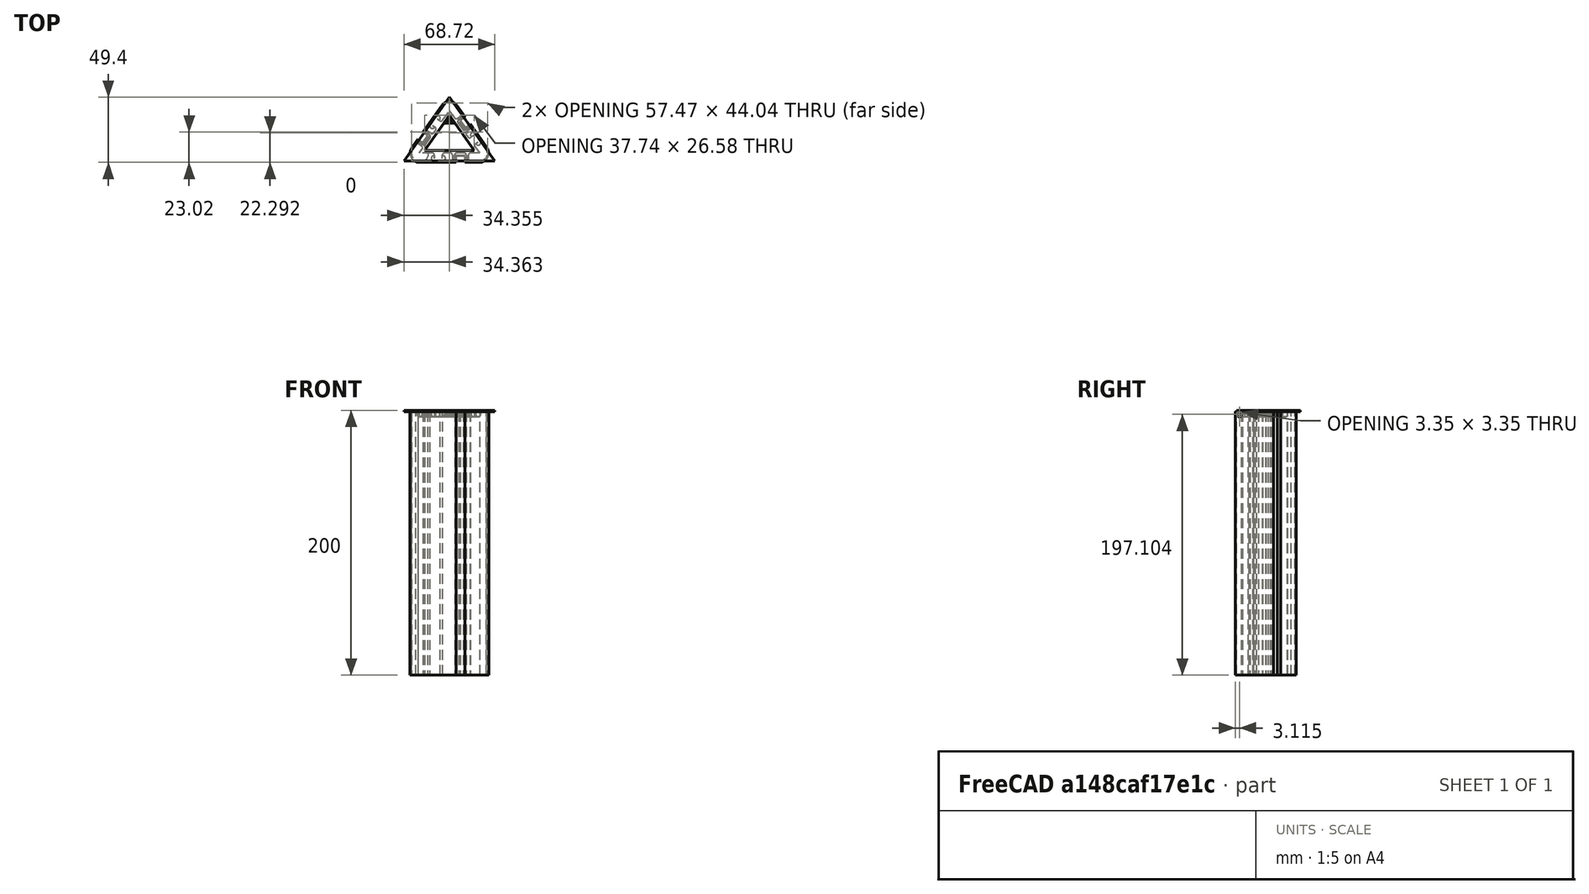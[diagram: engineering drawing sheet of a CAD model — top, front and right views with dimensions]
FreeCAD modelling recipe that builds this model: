
FCSTD DOCUMENT  (FreeCAD 0.20R29177 +233 (Git))
Label: tmp
License: All rights reserved
LicenseURL: http://en.wikipedia.org/wiki/All_rights_reserved
objects: Part::Part2DObjectPython×69, Part::Extrusion×29, Part::Cut×16, Part::MultiFuse×10, Part::Feature×9, Part::FeaturePython×5, App::DocumentObjectGroup×1, Part::Refine×1
note: 139 computed .brp shape members not serialized (recipe doc carries the construction recipe); baked Part::Feature solids carry a one-line shape summary decoded from their .brp

FEATURE [Part::Part2DObjectPython] Line219  label="Line220"  # Draft 2D object (typed FeaturePython)
  ChamferSize = 0
  Closed = false
  End = (11.2032,0.299498,-125.386)
  FilletRadius = 0
  Length = 52.293
  MakeFace = true
  Placement = pos=(-19.0727,42.9367,-125.386) rot=(0,0,1;3.14159rad)
  Points = (2) [(0,0,0),(-30.2758,42.6372,0)]
  Start = (-19.0727,42.9367,-125.386)
  Subdivisions = 0
FEATURE [Part::Part2DObjectPython] Line218  label="Line219"  # Draft 2D object (typed FeaturePython)
  ChamferSize = 0
  Closed = false
  End = (-19.0639,42.9441,-125.386)
  FilletRadius = 0
  Length = 52.293
  MakeFace = true
  Placement = pos=(-49.3293,0.299498,-125.386) rot=(0,0,1;3.14159rad)
  Points = (2) [(0,0,0),(-30.2654,-42.6446,0)]
  Start = (-49.3293,0.299498,-125.386)
  Subdivisions = 0
FEATURE [Part::Part2DObjectPython] Line217  label="Line218"  # Draft 2D object (typed FeaturePython)
  ChamferSize = 0
  Closed = false
  End = (11.2032,0.299498,-125.386)
  FilletRadius = 0
  Length = 60.5325
  MakeFace = true
  Placement = pos=(-49.3293,0.299498,-125.386) rot=(0,0,1;3.14159rad)
  Points = (2) [(0,0,0),(-60.5325,0,0)]
  Start = (-49.3293,0.299498,-125.386)
  Subdivisions = 0
FEATURE [Part::Feature] Fusion002009002005002004028003007012002019001002001013004001001
  shape: bbox 48.16 x 37.82 x 3.8 mm, 89 faces (baked)
FEATURE [Part::Feature] Face
  shape: bbox 3.474 x 4.892 x 3.8 mm, 1 faces, 0 solids (baked)
FEATURE [Part::Feature] Face001
  shape: bbox 3.473 x 4.893 x 3.8 mm, 1 faces, 0 solids (baked)
FEATURE [Part::Feature] Face002
  shape: bbox 6 x 2.493e-06 x 3.8 mm, 1 faces, 0 solids (baked)
FEATURE [Part::Feature] Face003
  Placement = pos=(1.78771e-08,-0.215137,-1.42e-14) rot=(0,0,1;0rad)
  shape: bbox 9.284 x 9.069 x 3.284 mm, 1 faces, 0 solids (baked)
FEATURE [Part::Feature] Face004
  Placement = pos=(0.175411,0.124556,0) rot=(0,0,1;0rad)
  shape: bbox 8.19 x 8.241 x 2.623e-06 mm, 1 faces, 0 solids (baked)
FEATURE [Part::Feature] Face005
  Placement = pos=(-0.175441,0.124513,0) rot=(0,0,1;0rad)
  shape: bbox 8.19 x 8.241 x 2.909e-06 mm, 1 faces, 0 solids (baked)
FEATURE [Part::Part2DObjectPython] Line220  label="Line221"  # Draft 2D object (typed FeaturePython)
  Area = 0
  ChamferSize = 0
  Closed = false
  End = (-53.4242,73.5903,-123.486)
  FilletRadius = 0
  Length = 75.6642
  MakeFace = true
  Placement = pos=(22.24,73.5903,-123.486) rot=(0,0.707107,-0.707107;3.14159rad)
  Points = (2) [(0,0,0),(75.6642,-3.1437e-06,-3.1437e-06)]
  Start = (22.24,73.5903,-123.486)
  Subdivisions = 0
FEATURE [Part::Part2DObjectPython] Line224  label="Line225"  # Draft 2D object (typed FeaturePython)
  Area = 0
  ChamferSize = 0
  Closed = true
  End = (-19.0714,121.994,-123.486)
  FilletRadius = 0
  Length = 59.3552
  MakeFace = true
  Placement = pos=(-19.0714,121.994,-123.486) rot=(-0.807496,-0.417103,0.417103;1.783rad)
  Points = (2) [(0,0,0),(0,0,0)]
  Start = (-19.0714,121.994,-123.486)
  Subdivisions = 0
FEATURE [Part::Part2DObjectPython] Line225  label="Line226"  # Draft 2D object (typed FeaturePython)
  Area = 0
  ChamferSize = 0
  Closed = false
  End = (-53.4242,73.5903,-123.486)
  FilletRadius = 0
  Length = 59.3552
  MakeFace = true
  Placement = pos=(-19.0714,121.994,-123.486) rot=(-0.807496,-0.417103,0.417103;1.783rad)
  Points = (2) [(0,0,0),(-59.3552,9.66338e-13,-1.20792e-12)]
  Start = (-19.0714,121.994,-123.486)
  Subdivisions = 0
FEATURE [Part::Part2DObjectPython] Line226  label="Line227"  # Draft 2D object (typed FeaturePython)
  Area = 0
  ChamferSize = 0
  Closed = true
  End = (-19.0714,121.994,-123.486)
  FilletRadius = 0
  Length = 0
  MakeFace = true
  Placement = pos=(-19.0714,121.994,-123.486) rot=(-0.807496,-0.417103,0.417103;1.783rad)
  Points = (2) [(0,0,0),(0,0,0)]
  Start = (-19.0714,121.994,-123.486)
  Subdivisions = 0
FEATURE [Part::Part2DObjectPython] Wire  # Draft 2D object (typed FeaturePython)
  Area = 1663.24
  ChamferSize = 0
  Closed = true
  End = (-19.0714,121.994,-123.486)
  FilletRadius = 0
  Length = 187.444
  MakeFace = true
  Placement = pos=(15.2992,73.5903,-123.486) rot=(0,0,1;0rad)
  Points = (3) [(0,0,0),(-68.7234,-6.72173e-12,-3.80851e-12),(-34.3706,48.4038,-3.85114e-12)]
  Start = (15.2992,73.5903,-123.486)
  Subdivisions = 0
FEATURE [Part::Extrusion] Extrusion006
  Base = -> Wire
  Dir = (-5.45e-14,3.88e-14,1)
  DirMode = 0
  FaceMakerClass = Part::FaceMakerBullseye
  LengthFwd = 0
  LengthRev = 0
  Solid = true
  Symmetric = false
FEATURE [Part::Part2DObjectPython] Wire001  # Draft 2D object (typed FeaturePython)
  Area = 501.678
  ChamferSize = 0
  Closed = true
  End = (-37.9365,81.5903,-123.486)
  FilletRadius = 0
  Length = 102.946
  MakeFace = true
  Placement = pos=(-19.0697,108.174,-123.486) rot=(1,0,0;3.14159rad)
  Points = (3) [(0,0,0),(18.8766,26.5837,2.18847e-12),(-18.8668,26.5837,1.56319e-13)]
  Start = (-19.0697,108.174,-123.486)
  Subdivisions = 0
FEATURE [Part::Extrusion] Extrusion007
  Base = -> Wire001
  Dir = (6.7e-15,-2.734e-13,57.9663)
  DirMode = 0
  FaceMakerClass = Part::FaceMakerBullseye
  LengthFwd = 0
  LengthRev = 0
  Solid = true
  Symmetric = false
FEATURE [Part::Cut] Cut
  Base = -> Extrusion006
  Tool = -> Extrusion007
FEATURE [Part::Part2DObjectPython] Rectangle  # Draft 2D object (typed FeaturePython)
  Area = 11871
  ChamferSize = 0
  Columns = 1
  FilletRadius = 0
  Height = 200
  Length = 59.3552
  MakeFace = true
  Placement = pos=(-53.4242,73.5903,-122.486) rot=(-0.807496,-0.417103,0.417103;1.783rad)
  Rows = 1
FEATURE [Part::Part2DObjectPython] Rectangle001  # Draft 2D object (typed FeaturePython)
  Area = 13744.7
  ChamferSize = 0
  Columns = 1
  FilletRadius = 0
  Height = 200
  Length = 68.7234
  MakeFace = true
  Placement = pos=(-53.4242,73.5903,-322.486) rot=(1,0,0;1.5708rad)
  Rows = 1
FEATURE [Part::Part2DObjectPython] Rectangle002  # Draft 2D object (typed FeaturePython)
  Area = 11813.7
  ChamferSize = 0
  Columns = 1
  FilletRadius = 0
  Height = 199
  Length = 59.3656
  MakeFace = true
  Placement = pos=(-19.0714,121.994,-123.486) rot=(-0.807581,0.417021,-0.417021;1.7829rad)
  Rows = 1
FEATURE [Part::Extrusion] Extrusion008
  Base = -> Rectangle001
  Dir = (9.82e-14,-1,4.1e-14)
  DirMode = 0
  FaceMakerClass = Part::FaceMakerBullseye
  LengthFwd = 0
  LengthRev = 0
  Solid = true
  Symmetric = false
FEATURE [Part::Extrusion] Extrusion009
  Base = -> Rectangle002
  Dir = (0.815352,0.578965,4.39e-14)
  DirMode = 0
  FaceMakerClass = Part::FaceMakerBullseye
  LengthFwd = 0
  LengthRev = 0
  Solid = true
  Symmetric = false
FEATURE [Part::Extrusion] Extrusion010
  Base = -> Rectangle
  Dir = (-0.815494,0.578766,-4.05e-14)
  DirMode = 0
  FaceMakerClass = Part::FaceMakerBullseye
  LengthFwd = 0
  LengthRev = 0
  Solid = true
  Symmetric = false
FEATURE [Part::MultiFuse] Fusion
  Shapes = -> [Extrusion010,Extrusion008,Extrusion009]
FEATURE [Part::Part2DObjectPython] Line228  label="Line229"  # Draft 2D object (typed FeaturePython)
  Area = 0
  ChamferSize = 0
  Closed = false
  End = (-38.3867,87.0032,-123.486)
  FilletRadius = 0
  Length = 1
  MakeFace = true
  Placement = pos=(-38.9655,86.1877,-123.486) rot=(0,0,1;0.953582rad)
  Points = (2) [(0,0,0),(1,-2.84217e-14,-2.84217e-14)]
  Start = (-38.9655,86.1877,-123.486)
  Subdivisions = 0
FEATURE [Part::Part2DObjectPython] Line230  label="Line231"  # Draft 2D object (typed FeaturePython)
  Area = 0
  ChamferSize = 0
  Closed = false
  End = (-34.6247,92.3039,-123.486)
  FilletRadius = 0
  Length = 1
  MakeFace = true
  Placement = pos=(-34.046,93.1194,-123.486) rot=(0,0,1;0.953582rad)
  Points = (2) [(0,0,0),(-1,5.68434e-14,2.41585e-13)]
  Start = (-34.046,93.1194,-123.486)
  Subdivisions = 0
FEATURE [Part::Part2DObjectPython] Rectangle006  # Draft 2D object (typed FeaturePython)
  Area = 29.25
  ChamferSize = 0
  Columns = 1
  FilletRadius = 0
  Height = 4.5
  Length = 6.5
  MakeFace = true
  Placement = pos=(-39.2022,87.582,-123.486) rot=(0,0,1;0.953582rad)
  Rows = 1
FEATURE [Part::Extrusion] Extrusion011
  Base = -> Rectangle006
  Dir = (1.04812e-11,6.8116e-12,-353.777)
  DirMode = 0
  FaceMakerClass = Part::FaceMakerBullseye
  LengthFwd = 0
  LengthRev = 0
  Solid = true
  Symmetric = false
FEATURE [Part::Cut] Cut001
  Base = -> Fusion
  Tool = -> Extrusion011
FEATURE [Part::Part2DObjectPython] Rectangle007  # Draft 2D object (typed FeaturePython)
  Area = 21476.5
  ChamferSize = 0
  Columns = 1
  FilletRadius = 0
  Height = 94.2802
  Length = 227.794
  MakeFace = true
  Placement = pos=(-179.415,55.7642,-123.486) rot=(0,0,1;0rad)
  Rows = 1
FEATURE [Part::FeaturePython] Slice  # WARN: FeaturePython — macro-defined, semantics opaque (R4)
  Base = -> Cut001
  Mode = 1
  Tolerance = 0
  Tools = -> [Rectangle007]
FEATURE [Part::FeaturePython] Slice_child1  label="Slice.1"  # WARN: FeaturePython — macro-defined, semantics opaque (R4)
  Base = -> Slice
  FilterType = 1
  Invert = false
  OverrideMaxVal = 0
  WindowFrom = 80
  WindowTo = 100
  items = 1
FEATURE [Part::FeaturePython] Slice_child2  label="Slice.2"  # WARN: FeaturePython — macro-defined, semantics opaque (R4)
  Base = -> Slice
  FilterType = 1
  Invert = false
  OverrideMaxVal = 0
  WindowFrom = 80
  WindowTo = 100
  items = 2
FEATURE [Part::FeaturePython] Slice_child4  label="Slice.4"  # WARN: FeaturePython — macro-defined, semantics opaque (R4)
  Base = -> Slice
  FilterType = 1
  Invert = false
  OverrideMaxVal = 0
  WindowFrom = 80
  WindowTo = 100
  items = 4
FEATURE [Part::FeaturePython] Slice_child5  label="Slice.5"  # WARN: FeaturePython — macro-defined, semantics opaque (R4)
  Base = -> Slice
  FilterType = 1
  Invert = false
  OverrideMaxVal = 0
  WindowFrom = 80
  WindowTo = 100
  items = 5
FEATURE [Part::Part2DObjectPython] Wire002  # Draft 2D object (typed FeaturePython)
  Area = 17.5
  ChamferSize = 0
  Closed = true
  End = (-39.11,95.4871,-123.486)
  FilletRadius = 0
  Length = 37
  MakeFace = true
  Placement = pos=(-38.5312,96.3026,-123.486) rot=(0,0,1;0.953582rad)
  Points = (8) [(0,0,0),(1.42109e-13,-5.5,-2.13163e-13),(-8.5,-5.5,-2.41585e-13),(-8.5,-2.70006e-13,2.70006e-13),(-7.5,-2.70006e-13,-2.55795e-13),+3 more]
  Start = (-38.5312,96.3026,-123.486)
  Subdivisions = 0
FEATURE [Part::Extrusion] Extrusion012
  Base = -> Wire002
  Dir = (-2.929e-13,9.0155e-12,-199)
  DirMode = 0
  FaceMakerClass = Part::FaceMakerBullseye
  LengthFwd = 0
  LengthRev = 0
  Solid = true
  Symmetric = false
FEATURE [Part::Part2DObjectPython] Line233  label="Line234"  # Draft 2D object (typed FeaturePython)
  Area = 0
  ChamferSize = 0
  Closed = false
  End = (-12.1534,104.479,-123.486)
  FilletRadius = 0
  Length = 1
  MakeFace = true
  Placement = pos=(-11.5744,103.664,-123.486) rot=(0,0,-1;0.953337rad)
  Points = (2) [(0,0,0),(-1,4.26326e-14,2.13163e-13)]
  Start = (-11.5744,103.664,-123.486)
  Subdivisions = 0
FEATURE [Part::Part2DObjectPython] Line234  label="Line235"  # Draft 2D object (typed FeaturePython)
  Area = 0
  ChamferSize = 0
  Closed = false
  End = (-7.81115,98.3639,-123.486)
  FilletRadius = 0
  Length = 1
  MakeFace = true
  Placement = pos=(-7.23218,97.5486,-123.486) rot=(0,0,-1;0.953337rad)
  Points = (2) [(0,0,0),(-1,4.9738e-14,2.13163e-13)]
  Start = (-7.23218,97.5486,-123.486)
  Subdivisions = 0
FEATURE [Part::Part2DObjectPython] Line237  label="Line238"  # Draft 2D object (typed FeaturePython)
  Area = 0
  ChamferSize = 0
  Closed = false
  End = (-7.08999,106.848,-123.486)
  FilletRadius = 0
  Length = 5.5
  MakeFace = true
  Placement = pos=(-11.5744,103.664,-123.486) rot=(0,0,-1;0.953337rad)
  Points = (2) [(0,0,0),(-1.56319e-13,5.5,-1.59162e-12)]
  Start = (-11.5744,103.664,-123.486)
  Subdivisions = 0
FEATURE [Part::Part2DObjectPython] Line238  label="Line239"  # Draft 2D object (typed FeaturePython)
  Area = 0
  ChamferSize = 0
  Closed = false
  End = (-3.32671,101.548,-123.486)
  FilletRadius = 0
  Length = 5.5
  MakeFace = true
  Placement = pos=(-7.81115,98.3639,-123.486) rot=(0,0,-1;0.953337rad)
  Points = (2) [(0,0,0),(-1.84741e-13,5.5,-2.25953e-12)]
  Start = (-7.81115,98.3639,-123.486)
  Subdivisions = 0
FEATURE [Part::Part2DObjectPython] Line239  label="Line240"  # Draft 2D object (typed FeaturePython)
  Area = 0
  ChamferSize = 0
  Closed = false
  End = (-3.5631,100.154,-123.486)
  FilletRadius = 0
  Length = 4.5
  MakeFace = true
  Placement = pos=(-7.23218,97.5486,-123.486) rot=(0,0,-1;0.953337rad)
  Points = (2) [(0,0,0),(-2.27374e-13,4.5,1.27898e-13)]
  Start = (-7.23218,97.5486,-123.486)
  Subdivisions = 0
FEATURE [Part::Part2DObjectPython] Line240  label="Line241"  # Draft 2D object (typed FeaturePython)
  Area = 0
  ChamferSize = 0
  Closed = false
  End = (-8.48431,107.084,-123.486)
  FilletRadius = 0
  Length = 4.5
  MakeFace = true
  Placement = pos=(-12.1534,104.479,-123.486) rot=(0,0,-1;0.953337rad)
  Points = (2) [(0,0,0),(-2.27374e-13,4.5,-2.27374e-13)]
  Start = (-12.1534,104.479,-123.486)
  Subdivisions = 0
FEATURE [Part::Part2DObjectPython] Rectangle008  # Draft 2D object (typed FeaturePython)
  Area = 35.75
  ChamferSize = 0
  Columns = 1
  FilletRadius = 0
  Height = 5.5
  Length = 6.5
  MakeFace = true
  Placement = pos=(-11.5744,103.664,-123.486) rot=(0,0,-1;0.953337rad)
  Rows = 1
FEATURE [Part::Extrusion] Extrusion
  Base = -> Rectangle008
  Dir = (8.0766e-12,-3.5936e-12,-250.551)
  DirMode = 0
  FaceMakerClass = Part::FaceMakerBullseye
  LengthFwd = 0
  LengthRev = 0
  Solid = true
  Symmetric = false
FEATURE [Part::Cut] Cut002
  Base = -> Slice_child5
  Tool = -> Extrusion
FEATURE [Part::Part2DObjectPython] Wire003  # Draft 2D object (typed FeaturePython)
  Area = 15.5
  ChamferSize = 0
  Closed = true
  End = (-3.5631,100.154,-123.486)
  FilletRadius = 0
  Length = 33
  MakeFace = true
  Placement = pos=(-7.23218,97.5486,-123.486) rot=(0,0,1;0rad)
  Points = (8) [(0,0,0),(-4.92121,6.93049,-1.84741e-13),(-1.25212,9.53584,-3.2685e-13),(-0.673157,8.72049,-1.02318e-12),(-3.52689,6.69411,-6.39488e-13),+3 more]
  Start = (-7.23218,97.5486,-123.486)
  Subdivisions = 0
FEATURE [Part::Extrusion] Extrusion013
  Base = -> Wire003
  Dir = (-7.6149e-12,-1.43446e-11,-199)
  DirMode = 0
  FaceMakerClass = Part::FaceMakerBullseye
  LengthFwd = 0
  LengthRev = 0
  Solid = true
  Symmetric = false
FEATURE [Part::Part2DObjectPython] Line221  label="Line222"  # Draft 2D object (typed FeaturePython)
  Area = 0
  ChamferSize = 0
  Closed = false
  End = (15.2992,73.5903,-123.486)
  FilletRadius = 0
  Length = 100
  MakeFace = true
  Placement = pos=(-42.5973,155.125,-123.486) rot=(-0.807581,0.417021,-0.417021;1.7829rad)
  Points = (2) [(0,0,0),(100,-8.1144e-12,1.86873e-12)]
  Start = (-42.5973,155.125,-123.486)
  Subdivisions = 0
FEATURE [Part::Part2DObjectPython] Line242  label="Line243"  # Draft 2D object (typed FeaturePython)
  Area = 0
  ChamferSize = 0
  Closed = false
  End = (-13.9631,78.0903,-123.486)
  FilletRadius = 0
  Length = 1
  MakeFace = true
  Placement = pos=(-14.9631,78.0903,-123.486) rot=(0,0,1;3.14159rad)
  Points = (2) [(0,0,0),(-1,-4.15481e-08,2.27374e-13)]
  Start = (-14.9631,78.0903,-123.486)
  Subdivisions = 0
FEATURE [Part::Part2DObjectPython] Line243  label="Line244"  # Draft 2D object (typed FeaturePython)
  Area = 0
  ChamferSize = 0
  Closed = false
  End = (-6.46309,78.0903,-123.486)
  FilletRadius = 0
  Length = 1
  MakeFace = true
  Placement = pos=(-7.46309,78.0903,-123.486) rot=(0,0,1;3.14159rad)
  Points = (2) [(0,0,0),(-1,-4.15481e-08,2.27374e-13)]
  Start = (-7.46309,78.0903,-123.486)
  Subdivisions = 0
FEATURE [Part::Part2DObjectPython] Line  # Draft 2D object (typed FeaturePython)
  Area = 0
  ChamferSize = 0
  Closed = false
  End = (-14.9631,73.5903,-123.486)
  FilletRadius = 0
  Length = 4.5
  MakeFace = true
  Placement = pos=(-14.9631,78.0903,-123.486) rot=(0,0,1;3.14159rad)
  Points = (2) [(0,0,0),(1.86967e-07,4.5,-1.40687e-12)]
  Start = (-14.9631,78.0903,-123.486)
  Subdivisions = 0
FEATURE [Part::Part2DObjectPython] Line244  label="Line245"  # Draft 2D object (typed FeaturePython)
  Area = 0
  ChamferSize = 0
  Closed = false
  End = (-6.46309,73.5903,-123.486)
  FilletRadius = 0
  Length = 4.5
  MakeFace = true
  Placement = pos=(-6.46309,78.0903,-123.486) rot=(0,0,1;3.14159rad)
  Points = (2) [(0,0,0),(1.86967e-07,4.5,-1.62004e-12)]
  Start = (-6.46309,78.0903,-123.486)
  Subdivisions = 0
FEATURE [Part::Part2DObjectPython] Line245  label="Line246"  # Draft 2D object (typed FeaturePython)
  Area = 0
  ChamferSize = 0
  Closed = false
  End = (-7.46309,72.5903,-123.486)
  FilletRadius = 0
  Length = 5.5
  MakeFace = true
  Placement = pos=(-7.46309,78.0903,-123.486) rot=(0,0,1;3.14159rad)
  Points = (2) [(0,0,0),(2.28515e-07,5.5,5.25802e-13)]
  Start = (-7.46309,78.0903,-123.486)
  Subdivisions = 0
FEATURE [Part::Part2DObjectPython] Line246  label="Line247"  # Draft 2D object (typed FeaturePython)
  Area = 0
  ChamferSize = 0
  Closed = false
  End = (-13.9631,72.5903,-123.486)
  FilletRadius = 0
  Length = 5.5
  MakeFace = true
  Placement = pos=(-13.9631,78.0903,-123.486) rot=(0,0,1;3.14159rad)
  Points = (2) [(0,0,0),(2.28515e-07,5.5,0)]
  Start = (-13.9631,78.0903,-123.486)
  Subdivisions = 0
FEATURE [Part::Part2DObjectPython] Line247  label="Line248"  # Draft 2D object (typed FeaturePython)
  Area = 0
  ChamferSize = 0
  Closed = false
  End = (-14.4631,77.0903,-123.486)
  FilletRadius = 0
  Length = 1
  MakeFace = true
  Placement = pos=(-14.4631,78.0903,-123.486) rot=(0,0,1;3.14159rad)
  Points = (2) [(0,0,0),(4.15481e-08,1,-3.12639e-13)]
  Start = (-14.4631,78.0903,-123.486)
  Subdivisions = 0
FEATURE [Part::Part2DObjectPython] Line249  label="Line250"  # Draft 2D object (typed FeaturePython)
  Area = 0
  ChamferSize = 0
  Closed = false
  End = (-13.9631,77.0903,-123.486)
  FilletRadius = 0
  Length = 6.5
  MakeFace = true
  Placement = pos=(-7.46309,77.0903,-123.486) rot=(0,0,1;3.14159rad)
  Points = (2) [(0,0,0),(6.5,-2.70063e-07,1.84741e-13)]
  Start = (-7.46309,77.0903,-123.486)
  Subdivisions = 0
FEATURE [Part::Part2DObjectPython] Rectangle009  # Draft 2D object (typed FeaturePython)
  Area = 29.25
  ChamferSize = 0
  Columns = 1
  FilletRadius = 0
  Height = 4.5
  Length = 6.5
  MakeFace = true
  Placement = pos=(-7.46309,77.0903,-123.486) rot=(0,0,1;3.14159rad)
  Rows = 1
FEATURE [Part::Extrusion] Extrusion014
  Base = -> Rectangle009
  Dir = (-9.5338e-12,8.731e-13,-292.184)
  DirMode = 0
  FaceMakerClass = Part::FaceMakerBullseye
  LengthFwd = 0
  LengthRev = 0
  Solid = true
  Symmetric = false
FEATURE [Part::Cut] Cut003
  Base = -> Slice_child4
  Tool = -> Extrusion014
FEATURE [Part::Part2DObjectPython] Wire004  # Draft 2D object (typed FeaturePython)
  Area = 15.5
  ChamferSize = 0
  Closed = true
  End = (-14.9631,73.5903,-123.486)
  FilletRadius = 0
  Length = 33
  MakeFace = true
  Placement = pos=(-14.9631,78.0903,-123.486) rot=(0,0,1;3.14159rad)
  Points = (8) [(0,0,0),(-8.5,2.18128e-07,-1.27898e-13),(-8.5,4.5,-1.74794e-12),(-7.5,4.5,9.9476e-14),(-7.5,1,-2.13163e-13),(-1,1,1.7053e-13),(-1,4.5,1.56319e-13),+1 more]
  Start = (-14.9631,78.0903,-123.486)
  Subdivisions = 0
FEATURE [Part::Extrusion] Extrusion015
  Base = -> Wire004
  Dir = (-6.1347e-12,3.55999e-11,-199)
  DirMode = 0
  FaceMakerClass = Part::FaceMakerBullseye
  LengthFwd = 0
  LengthRev = 0
  Solid = true
  Symmetric = false
FEATURE [Part::MultiFuse] Fusion002009002005002004028003007012002019001002001013004001002
  Shapes = -> [Extrusion015,Cut003,Extrusion012,Extrusion013]
FEATURE [Part::MultiFuse] Fusion002009002005002004028003007012002019001002001013004001003
  Shapes = -> [Fusion002009002005002004028003007012002019001002001013004001002,Cut002,Slice_child1]
FEATURE [Part::MultiFuse] Fusion002009002005002004028003007012002019001002001013004001004
  Shapes = -> [Fusion002009002005002004028003007012002019001002001013004001003,Slice_child2]
FEATURE [Part::Part2DObjectPython] Wire005  # Draft 2D object (typed FeaturePython)
  Area = 0.407747
  ChamferSize = 0
  Closed = true
  End = (-53.4242,73.5903,-123.486)
  FilletRadius = 0
  Length = 3.77694
  MakeFace = true
  Placement = pos=(-54.2397,74.169,-123.486) rot=(0,0,-1;0.617214rad)
  Points = (3) [(0,0,0),(1.57877,-0.815494,0),(1,-7.10543e-15,0)]
  Start = (-54.2397,74.169,-123.486)
  Subdivisions = 0
FEATURE [Part::Part2DObjectPython] Wire006  # Draft 2D object (typed FeaturePython)
  Area = 0.407676
  ChamferSize = 0
  Closed = true
  End = (15.2992,73.5903,-123.486)
  FilletRadius = 0
  Length = 3.77706
  MakeFace = true
  Placement = pos=(16.1146,74.1692,-123.486) rot=(0,0,-1;0.617214rad)
  Points = (3) [(0,0,0),(0.248936,-1.75953,2.77112e-12),(-0.329829,-0.944041,-4.26326e-14)]
  Start = (16.1146,74.1692,-123.486)
  Subdivisions = 0
FEATURE [Part::Part2DObjectPython] Wire007  # Draft 2D object (typed FeaturePython)
  Area = 0.47202
  ChamferSize = 0
  Closed = true
  End = (-19.0714,121.994,-123.486)
  FilletRadius = 0
  Length = 3.63085
  MakeFace = true
  Placement = pos=(-19.8869,122.573,-123.486) rot=(0,0,-1;0.617214rad)
  Points = (3) [(0,0,0),(1.32983,0.944041,-1.73372e-12),(1,9.9476e-13,-1.77636e-12)]
  Start = (-19.8869,122.573,-123.486)
  Subdivisions = 0
FEATURE [Part::Extrusion] Extrusion016
  Base = -> Wire006
  Dir = (4.08027e-10,-5.59542e-10,-199)
  DirMode = 0
  FaceMakerClass = Part::FaceMakerBullseye
  LengthFwd = 0
  LengthRev = 0
  Solid = true
  Symmetric = false
FEATURE [Part::Extrusion] Extrusion017
  Base = -> Wire005
  Dir = (2.25e-14,3.937e-13,-199)
  DirMode = 0
  FaceMakerClass = Part::FaceMakerBullseye
  LengthFwd = 0
  LengthRev = 0
  Solid = true
  Symmetric = false
FEATURE [Part::Extrusion] Extrusion018
  Base = -> Wire007
  Dir = (-2.11569e-10,3.1303e-10,-199)
  DirMode = 0
  FaceMakerClass = Part::FaceMakerBullseye
  LengthFwd = 0
  LengthRev = 0
  Solid = true
  Symmetric = false
FEATURE [Part::MultiFuse] Fusion002009002005002004028003007012002019001002001013004001005
  Shapes = -> [Fusion002009002005002004028003007012002019001002001013004001004,Extrusion017]
FEATURE [Part::MultiFuse] Fusion002009002005002004028003007012002019001002001013004001006
  Shapes = -> [Fusion002009002005002004028003007012002019001002001013004001005,Extrusion018]
FEATURE [Part::MultiFuse] Fusion002009002005002004028003007012002019001002001013004001007
  Shapes = -> [Fusion002009002005002004028003007012002019001002001013004001006,Extrusion016]
FEATURE [Part::Part2DObjectPython] Circle  # Draft 2D object (typed FeaturePython)
  Area = 3.14159
  FirstAngle = 0
  LastAngle = 0
  MakeFace = true
  Placement = pos=(15.2992,73.5903,-123.486) rot=(0,0,1;0rad)
  Radius = 1
FEATURE [Part::Part2DObjectPython] Circle001  # Draft 2D object (typed FeaturePython)
  Area = 3.14159
  FirstAngle = 0
  LastAngle = 0
  MakeFace = true
  Placement = pos=(-53.4242,73.5903,-123.486) rot=(0,0,1;0rad)
  Radius = 1
FEATURE [Part::Part2DObjectPython] Circle002  # Draft 2D object (typed FeaturePython)
  Area = 3.14159
  FirstAngle = 0
  LastAngle = 0
  MakeFace = true
  Placement = pos=(-19.0714,121.994,-123.486) rot=(0,0,1;0rad)
  Radius = 1
FEATURE [Part::Part2DObjectPython] Circle003  # Draft 2D object (typed FeaturePython)
  Area = 113.097
  FirstAngle = 0
  LastAngle = 0
  MakeFace = true
  Placement = pos=(3.67995,79.5903,-123.486) rot=(0,0,1;0rad)
  Radius = 6
FEATURE [Part::Part2DObjectPython] Circle004  # Draft 2D object (typed FeaturePython)
  Area = 153.938
  FirstAngle = 0
  LastAngle = 0
  MakeFace = true
  Placement = pos=(3.67995,79.5903,-123.486) rot=(0,0,1;0rad)
  Radius = 7
FEATURE [Part::Extrusion] Extrusion022
  Base = -> Circle004
  Dir = (-1.871e-13,2.726e-13,-199)
  DirMode = 0
  FaceMakerClass = Part::FaceMakerBullseye
  LengthFwd = 0
  LengthRev = 0
  Solid = true
  Symmetric = false
FEATURE [Part::Extrusion] Extrusion023
  Base = -> Circle003
  Dir = (-3.395e-13,4.948e-13,-361.137)
  DirMode = 0
  FaceMakerClass = Part::FaceMakerBullseye
  LengthFwd = 0
  LengthRev = 0
  Solid = true
  Symmetric = false
FEATURE [Part::Cut] Cut004
  Base = -> Extrusion022
  Tool = -> Extrusion023
FEATURE [Part::Part2DObjectPython] Line250  label="Line251"  # Draft 2D object (typed FeaturePython)
  Area = 0
  ChamferSize = 0
  Closed = false
  End = (9.38741,83.643,-322.486)
  FilletRadius = 0
  Length = 7
  MakeFace = true
  Placement = pos=(3.67995,79.5903,-322.486) rot=(1,0,0;3.14159rad)
  Points = (2) [(0,0,0),(5.70746,-4.05276,6.9349e-12)]
  Start = (3.67995,79.5903,-322.486)
  Subdivisions = 0
FEATURE [Part::Part2DObjectPython] Line251  label="Line252"  # Draft 2D object (typed FeaturePython)
  Area = 0
  ChamferSize = 0
  Closed = false
  End = (3.67995,72.5903,-322.486)
  FilletRadius = 0
  Length = 7
  MakeFace = true
  Placement = pos=(3.67995,79.5903,-322.486) rot=(1,0,0;3.14159rad)
  Points = (2) [(0,0,0),(-8.40923e-11,7,2.84217e-13)]
  Start = (3.67995,79.5903,-322.486)
  Subdivisions = 0
FEATURE [Part::Part2DObjectPython] Wire008  # Draft 2D object (typed FeaturePython)
  Area = 133.226
  ChamferSize = 0
  Closed = true
  End = (9.38741,83.643,-322.486)
  FilletRadius = 0
  Length = 57.0494
  MakeFace = true
  Placement = pos=(3.67995,72.5903,-322.486) rot=(1,0,0;3.14159rad)
  Points = (3) [(0,0,0),(21.9308,4.215,0),(5.70746,-11.0528,6.65068e-12)]
  Start = (3.67995,72.5903,-322.486)
  Subdivisions = 0
FEATURE [Part::Extrusion] Extrusion024
  Base = -> Wire008
  Dir = (1.52045e-11,1.77155e-10,301.099)
  DirMode = 0
  FaceMakerClass = Part::FaceMakerBullseye
  LengthFwd = 0
  LengthRev = 0
  Solid = true
  Symmetric = false
FEATURE [Part::Cut] Cut005
  Base = -> Fusion002009002005002004028003007012002019001002001013004001007
  Tool = -> Extrusion024
FEATURE [Part::Part2DObjectPython] Line252  label="Line253"  # Draft 2D object (typed FeaturePython)
  Area = 0
  ChamferSize = 0
  Closed = false
  End = (-24.7766,115.683,-123.486)
  FilletRadius = 0
  Length = 7
  MakeFace = true
  Placement = pos=(-19.0701,111.629,-123.486) rot=(0,0,1;0rad)
  Points = (2) [(0,0,0),(-5.70651,4.0541,0)]
  Start = (-19.0701,111.629,-123.486)
  Subdivisions = 0
FEATURE [Part::Part2DObjectPython] Line253  label="Line254"  # Draft 2D object (typed FeaturePython)
  Area = 0
  ChamferSize = 0
  Closed = false
  End = (-13.3627,115.682,-123.486)
  FilletRadius = 0
  Length = 7
  MakeFace = true
  Placement = pos=(-19.0701,111.629,-123.486) rot=(0,0,1;0rad)
  Points = (2) [(0,0,0),(5.70746,4.05276,-1.10845e-12)]
  Start = (-19.0701,111.629,-123.486)
  Subdivisions = 0
FEATURE [Part::Part2DObjectPython] Line254  label="Line255"  # Draft 2D object (typed FeaturePython)
  Area = 0
  ChamferSize = 0
  Closed = false
  End = (-41.8084,72.5903,-123.486)
  FilletRadius = 0
  Length = 7
  MakeFace = true
  Placement = pos=(-41.8084,79.5903,-123.486) rot=(0,0,1;0rad)
  Points = (2) [(0,0,0),(6.82121e-13,-7,0)]
  Start = (-41.8084,79.5903,-123.486)
  Subdivisions = 0
FEATURE [Part::Part2DObjectPython] Line255  label="Line256"  # Draft 2D object (typed FeaturePython)
  Area = 0
  ChamferSize = 0
  Closed = false
  End = (-47.5168,83.6416,-123.486)
  FilletRadius = 0
  Length = 7
  MakeFace = true
  Placement = pos=(-41.8084,79.5903,-123.486) rot=(0,0,1;0rad)
  Points = (2) [(0,0,0),(-5.70846,4.05136,9.9476e-14)]
  Start = (-41.8084,79.5903,-123.486)
  Subdivisions = 0
FEATURE [Part::Part2DObjectPython] Wire009  # Draft 2D object (typed FeaturePython)
  Area = 116.676
  ChamferSize = 0
  Closed = true
  End = (-41.8084,72.5903,-123.486)
  FilletRadius = 0
  Length = 51.9976
  MakeFace = true
  Placement = pos=(-47.5168,83.6416,-123.486) rot=(0,0,1;0rad)
  Points = (3) [(0,0,0),(-13.4387,-14.8614,-1.42109e-14),(5.70846,-11.0514,-8.52651e-14)]
  Start = (-47.5168,83.6416,-123.486)
  Subdivisions = 0
FEATURE [Part::Part2DObjectPython] Wire010  # Draft 2D object (typed FeaturePython)
  Area = 64.0628
  ChamferSize = 0
  Closed = true
  End = (-13.3627,115.682,-123.486)
  FilletRadius = 0
  Length = 36.6012
  MakeFace = true
  Placement = pos=(-24.7766,115.683,-123.486) rot=(0,0,1;0rad)
  Points = (3) [(0,0,0),(5.87287,11.2246,1.42109e-14),(11.414,-0.0013408,-1.12266e-12)]
  Start = (-24.7766,115.683,-123.486)
  Subdivisions = 0
FEATURE [Part::Extrusion] Extrusion025
  Base = -> Wire010
  Dir = (-1.97591e-11,1.07649e-11,-199)
  DirMode = 0
  FaceMakerClass = Part::FaceMakerBullseye
  LengthFwd = 0
  LengthRev = 0
  Solid = true
  Symmetric = false
FEATURE [Part::Extrusion] Extrusion026
  Base = -> Wire009
  Dir = (-1.1338e-12,1.319e-12,-199)
  DirMode = 0
  FaceMakerClass = Part::FaceMakerBullseye
  LengthFwd = 0
  LengthRev = 0
  Solid = true
  Symmetric = false
FEATURE [Part::Cut] Cut006
  Base = -> Cut005
  Tool = -> Extrusion026
FEATURE [Part::Cut] Cut007
  Base = -> Cut006
  Tool = -> Extrusion025
FEATURE [Part::Part2DObjectPython] Circle005  # Draft 2D object (typed FeaturePython)
  Area = 153.938
  FirstAngle = 0
  LastAngle = 0
  MakeFace = true
  Placement = pos=(-41.8084,79.5903,-123.486) rot=(0,0,1;0rad)
  Radius = 7
FEATURE [Part::Part2DObjectPython] Circle006  # Draft 2D object (typed FeaturePython)
  Area = 113.097
  FirstAngle = 0
  LastAngle = 0
  MakeFace = true
  Placement = pos=(-41.8084,79.5903,-123.486) rot=(0,0,1;0rad)
  Radius = 6
FEATURE [Part::Part2DObjectPython] Circle007  # Draft 2D object (typed FeaturePython)
  Area = 153.938
  FirstAngle = 0
  LastAngle = 0
  MakeFace = true
  Placement = pos=(-19.0701,111.629,-123.486) rot=(0,0,1;0rad)
  Radius = 7
FEATURE [Part::Part2DObjectPython] Circle008  # Draft 2D object (typed FeaturePython)
  Area = 113.097
  FirstAngle = 0
  LastAngle = 0
  MakeFace = true
  Placement = pos=(-19.0701,111.629,-123.486) rot=(0,0,1;0rad)
  Radius = 6
FEATURE [Part::Extrusion] Extrusion027
  Base = -> Circle007
  Dir = (-1.871e-13,2.726e-13,-199)
  DirMode = 0
  FaceMakerClass = Part::FaceMakerBullseye
  LengthFwd = 0
  LengthRev = 0
  Solid = true
  Symmetric = false
FEATURE [Part::Extrusion] Extrusion028
  Base = -> Circle005
  Dir = (-1.871e-13,2.726e-13,-199)
  DirMode = 0
  FaceMakerClass = Part::FaceMakerBullseye
  LengthFwd = 0
  LengthRev = 0
  Solid = true
  Symmetric = false
FEATURE [Part::Extrusion] Extrusion029
  Base = -> Circle006
  Dir = (-9.882e-13,1.4403e-12,-1051.29)
  DirMode = 0
  FaceMakerClass = Part::FaceMakerBullseye
  LengthFwd = 0
  LengthRev = 0
  Solid = true
  Symmetric = false
FEATURE [Part::Extrusion] Extrusion030
  Base = -> Circle008
  Dir = (-2.649e-13,3.861e-13,-281.804)
  DirMode = 0
  FaceMakerClass = Part::FaceMakerBullseye
  LengthFwd = 0
  LengthRev = 0
  Solid = true
  Symmetric = false
FEATURE [Part::Cut] Cut008
  Base = -> Extrusion027
  Tool = -> Extrusion030
FEATURE [Part::Cut] Cut009
  Base = -> Extrusion028
  Tool = -> Extrusion029
FEATURE [Part::Part2DObjectPython] Wire011  # Draft 2D object (typed FeaturePython)
  Area = 370.625
  ChamferSize = 0
  Closed = true
  End = (-37.7157,95.7238,-123.486)
  FilletRadius = 0
  Length = 84.7749
  MakeFace = true
  Placement = pos=(-14.9631,73.5903,-123.486) rot=(0,0,1;0rad)
  Points = (4) [(0,0,0),(-26.8453,-2.6148e-12,1.50635e-12),(-31.7383,9.47259,1.49214e-12),(-22.7526,22.1336,1.56319e-12)]
  Start = (-14.9631,73.5903,-123.486)
  Subdivisions = 0
FEATURE [Part::Extrusion] Extrusion031
  Base = -> Wire011
  Dir = (-1.49617e-11,5.0365e-12,-296.251)
  DirMode = 0
  FaceMakerClass = Part::FaceMakerBullseye
  LengthFwd = 0
  LengthRev = 0
  Solid = true
  Symmetric = false
FEATURE [Part::Cut] Cut010
  Base = -> Cut009
  Tool = -> Extrusion031
FEATURE [Part::MultiFuse] Fusion002009002005002004028003007012002019001002001013004001008
  Shapes = -> [Cut007,Cut010]
FEATURE [Part::Part2DObjectPython] Wire012  # Draft 2D object (typed FeaturePython)
  Area = 351.682
  ChamferSize = 0
  Closed = true
  End = (4.19633,73.5903,-123.486)
  FilletRadius = 0
  Length = 79.7309
  MakeFace = true
  Placement = pos=(-14.9631,73.5903,-123.486) rot=(0,0,1;0rad)
  Points = (4) [(0,0,0),(11.4,26.5636,1.5774e-12),(23.8341,9.05276,-1.03739e-12),(19.1594,1.86162e-12,1.5774e-12)]
  Start = (-14.9631,73.5903,-123.486)
  Subdivisions = 0
FEATURE [Part::Extrusion] Extrusion032
  Base = -> Wire012
  Dir = (-4.4377e-12,1.11758e-11,-255.943)
  DirMode = 0
  FaceMakerClass = Part::FaceMakerBullseye
  LengthFwd = 0
  LengthRev = 0
  Solid = true
  Symmetric = false
FEATURE [Part::Cut] Cut011
  Base = -> Cut004
  Tool = -> Extrusion032
FEATURE [Part::MultiFuse] Fusion002009002005002004028003007012002019001002001013004001009
  Shapes = -> [Fusion002009002005002004028003007012002019001002001013004001008,Cut011]
FEATURE [Part::Part2DObjectPython] Wire013  # Draft 2D object (typed FeaturePython)
  Area = 373.426
  ChamferSize = 0
  Closed = true
  End = (-14.178,115.103,-123.486)
  FilletRadius = 0
  Length = 86.3119
  MakeFace = true
  Placement = pos=(-3.5631,100.154,-123.486) rot=(0,0,1;0rad)
  Points = (4) [(0,0,0),(-34.1526,-4.43005,-1.42109e-14),(-20.389,14.9434,-1.42109e-14),(-10.6149,14.9489,-1.91847e-12)]
  Start = (-3.5631,100.154,-123.486)
  Subdivisions = 0
FEATURE [Part::Extrusion] Extrusion033
  Base = -> Wire013
  Dir = (-9.019e-13,-1.28108e-11,-279.005)
  DirMode = 0
  FaceMakerClass = Part::FaceMakerBullseye
  LengthFwd = 0
  LengthRev = 0
  Solid = true
  Symmetric = false
FEATURE [Part::Cut] Cut012
  Base = -> Cut008
  Tool = -> Extrusion033
FEATURE [Part::MultiFuse] Fusion002009002005002004028003007012002019001002001013004001010
  Shapes = -> [Cut012,Fusion002009002005002004028003007012002019001002001013004001009]
FEATURE [App::DocumentObjectGroup] GrExplode_Slice  label="Exploded Slice"
  Group = -> [Fusion002009002005002004028003007012002019001002001013004001010]
FEATURE [Part::Feature] Fusion002009002005002004028003007012002019001002001013004001010_solid  label="Fusion002009002005002004028003007012002019001002001013004001010 (Solid)"
  shape: bbox 59.49 x 46.04 x 199 mm, 106 faces (baked)
FEATURE [Part::Refine] Fusion002009002005002004028003007012002019001002001013004001010001
  Source = -> Fusion002009002005002004028003007012002019001002001013004001010
FEATURE [Part::Feature] Fusion002009002005002004028003007012002019001002001013004001010001001
  shape: bbox 59.49 x 46.04 x 199 mm, 49 faces (baked)
FEATURE [Part::Part2DObjectPython] Circle009  # Draft 2D object (typed FeaturePython)
  Area = 3.14159
  FirstAngle = 0
  LastAngle = 0
  MakeFace = true
  Placement = pos=(-39.2022,87.582,-123.486) rot=(0,0,1;0rad)
  Radius = 1
FEATURE [Part::Part2DObjectPython] Circle010  # Draft 2D object (typed FeaturePython)
  Area = 6.28319
  FirstAngle = 0
  LastAngle = 0
  MakeFace = true
  Placement = pos=(-39.2022,87.582,-123.486) rot=(0,0,1;0rad)
  Radius = 1.41421
FEATURE [Part::Extrusion] Extrusion034
  Base = -> Circle010
  Dir = (-4.4716e-12,-2.4249e-12,-199)
  DirMode = 0
  FaceMakerClass = Part::FaceMakerBullseye
  LengthFwd = 0
  LengthRev = 0
  Solid = true
  Symmetric = false
FEATURE [Part::Extrusion] Extrusion035
  Base = -> Circle009
  Dir = (-4.502e-12,-2.4414e-12,-200.351)
  DirMode = 0
  FaceMakerClass = Part::FaceMakerBullseye
  LengthFwd = 0
  LengthRev = 0
  Solid = true
  Symmetric = false
FEATURE [Part::Cut] Cut013
  Base = -> Extrusion034
  Tool = -> Extrusion035
FEATURE [Part::Part2DObjectPython] Line256  label="Line257"  # Draft 2D object (typed FeaturePython)
  Area = 0
  ChamferSize = 0
  Closed = false
  End = (-37.5712,86.4244,-123.486)
  FilletRadius = 0
  Length = 2
  MakeFace = true
  Placement = pos=(-39.2022,87.582,-123.486) rot=(0,0,1;0rad)
  Points = (2) [(0,0,0),(1.63099,-1.15753,2.84217e-14)]
  Start = (-39.2022,87.582,-123.486)
  Subdivisions = 0
FEATURE [Part::Part2DObjectPython] Line257  label="Line258"  # Draft 2D object (typed FeaturePython)
  Area = 0
  ChamferSize = 0
  Closed = false
  End = (-40.3597,85.951,-123.486)
  FilletRadius = 0
  Length = 2
  MakeFace = true
  Placement = pos=(-39.2022,87.582,-123.486) rot=(0,0,1;0rad)
  Points = (2) [(0,0,0),(-1.15753,-1.63099,2.84217e-14)]
  Start = (-39.2022,87.582,-123.486)
  Subdivisions = 0
FEATURE [Part::Part2DObjectPython] Wire014  # Draft 2D object (typed FeaturePython)
  Area = 15.3695
  ChamferSize = 0
  Closed = true
  End = (-39.2022,87.582,-123.486)
  FilletRadius = 0
  Length = 21.5549
  MakeFace = true
  Placement = pos=(-37.5712,86.4244,-123.486) rot=(0,0,1;0rad)
  Points = (6) [(0,0,0),(1.06549,3.22912,1.56319e-13),(0.250001,3.80789,2.41585e-13),(-7.62317,0.489583,1.73372e-12),(-2.44949,0.00424863,-2.84217e-14),+1 more]
  Start = (-37.5712,86.4244,-123.486)
  Subdivisions = 0
FEATURE [Part::Extrusion] Extrusion036
  Base = -> Wire014
  Dir = (-6.69323e-11,4.12248e-11,-245.263)
  DirMode = 0
  FaceMakerClass = Part::FaceMakerBullseye
  LengthFwd = 0
  LengthRev = 0
  Solid = true
  Symmetric = false
FEATURE [Part::Cut] Cut014
  Base = -> Cut013
  Tool = -> Extrusion036
FEATURE [Part::Cut] Cut015
  Base = -> Fusion002009002005002004028003007012002019001002001013004001010001001
  Tool = -> Cut014
FEATURE [Part::Part2DObjectPython] Circle011  # Draft 2D object (typed FeaturePython)
  Area = 314.159
  FirstAngle = 0
  LastAngle = 0
  MakeFace = true
  Placement = pos=(-31.9433,105.585,-222.986) rot=(-0.807496,-0.417103,0.417103;1.783rad)
  Radius = 10
FEATURE [Part::Part2DObjectPython] Line258  label="Line259"  # Draft 2D object (typed FeaturePython)
  Area = 0
  ChamferSize = 0
  Closed = false
  End = (-31.9433,105.585,-141.734)
  FilletRadius = 0
  Length = 162.505
  MakeFace = true
  Placement = pos=(-31.9433,105.585,-304.239) rot=(-0.807496,-0.417103,0.417103;1.783rad)
  Points = (2) [(0,0,0),(-1.04734e-10,-162.505,-4.0373e-11)]
  Start = (-31.9433,105.585,-304.239)
  Subdivisions = 0
FEATURE [Part::Part2DObjectPython] Line259  label="Line260"  # Draft 2D object (typed FeaturePython)
  Area = 0
  ChamferSize = 0
  Closed = false
  End = (-56.9063,70.4117,-222.986)
  FilletRadius = 0
  Length = 86.2628
  MakeFace = true
  Placement = pos=(-6.98032,140.759,-222.986) rot=(-0.807496,-0.417103,0.417103;1.783rad)
  Points = (2) [(0,0,0),(-86.2628,4.06146e-11,-5.50386e-11)]
  Start = (-6.98032,140.759,-222.986)
  Subdivisions = 0
FEATURE [Part::Part2DObjectPython] Wire015  # Draft 2D object (typed FeaturePython)
  Area = 200
  ChamferSize = 0
  Closed = true
  End = (-37.731,97.4302,-222.986)
  FilletRadius = 0
  Length = 56.5685
  MakeFace = true
  Placement = pos=(-31.9433,105.585,-212.986) rot=(-0.807496,-0.417103,0.417103;1.783rad)
  Points = (4) [(0,0,0),(10,10,-1.42109e-14),(1.2875e-11,20,-1.42109e-14),(-10,10,1.42109e-14)]
  Start = (-31.9433,105.585,-212.986)
  Subdivisions = 0
